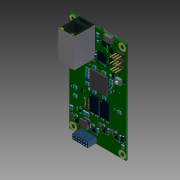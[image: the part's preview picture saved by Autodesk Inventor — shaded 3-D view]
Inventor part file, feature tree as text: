
AUTODESK INVENTOR PART (.ipt)
format: ipt  version: 2013 (Build 170138000, 138)  size: 6,881,792 bytes
history: native  units: in
note: dims shown in document units (in); Inventor stores cm internally (conversion verified against a paired STEP export)
features: imported_body x1163, extrude x1112, other x52, projected_geometry x21, sketch x2
ambient origin geometry x8: Origin, YZ Plane, XZ Plane, XY Plane, X Axis, Y Axis, Z Axis, Center Point
feature tree (2350):
  other  "Board"
  other  "Repaired Geometry1"
  sketch  "Sketch1"  dims[d3=0.3009in d4=0.0005in d5=0.0653in d6=0.0653in d7=0.0653in d8=0.0653in d9=0.0653in d10=0.0653in d11=0.0653in d12=0.0653in d13=0.0098in d14=0.0098in d15=1.1299in d16=1.1299in d17=1.7402in d18=0.0404in]
  extrude  "Extruded"  Depth=0.0005in
  extrude  "Extruded_1"  Depth=0.0653in
  extrude  "Extruded_2"  Depth=0.0653in
  extrude  "Extruded_3"  Depth=0.0653in
  extrude  "Extruded_4"  Depth=0.0653in
  extrude  "Extruded_5"  Depth=0.0653in
  extrude  "Extruded_6"  Depth=0.0653in
  extrude  "Extruded_7"  Depth=0.0653in
  extrude  "Extruded_8"  Depth=0.0653in
  extrude  "Extruded_9"  Depth=0.0098in
  extrude  "Extruded_10"  Depth=0.0098in
  extrude  "Extruded_11"  Depth=1.1299in
  extrude  "Extruded_12"  Depth=1.1299in
  extrude  "Extruded_13"  Depth=1.7402in
  extrude  "Extruded_14"  Depth=0.0404in
  extrude  "Extruded_15"  [1 undecoded]
  extrude  "Extruded_16"  [1 undecoded]
  extrude  "Extruded_17"  [1 undecoded]
  extrude  "Extruded_18"  [1 undecoded]
  extrude  "Extruded_19"  [1 undecoded]
  extrude  "Extruded_20"  [1 undecoded]
  extrude  "Extruded_21"  [1 undecoded]
  extrude  "Extruded_22"  [1 undecoded]
  extrude  "Extruded_23"  [1 undecoded]
  extrude  "Extruded_24"  [1 undecoded]
  extrude  "Extruded_25"  [1 undecoded]
  extrude  "Extruded_26"  [1 undecoded]
  extrude  "Extruded_27"  [1 undecoded]
  other  "Cylinder"
  other  "Cylinder_1"
  other  "Cylinder_2"
  other  "Cylinder_3"
  extrude  "Extruded_28"  [1 undecoded]
  extrude  "Extruded_29"  [1 undecoded]
  other  "Cylinder_4"
  extrude  "Extruded_30"  [1 undecoded]
  other  "Cylinder_5"
  extrude  "Extruded_31"  [1 undecoded]
  other  "Cylinder_6"
  other  "Cylinder_7"
  extrude  "Extruded_32"  [1 undecoded]
  extrude  "Extruded_33"  [1 undecoded]
  extrude  "Extruded_34"  [1 undecoded]
  extrude  "Extruded_35"  [1 undecoded]
  extrude  "Extruded_36"  [1 undecoded]
  extrude  "Extruded_37"  [1 undecoded]
  extrude  "Extruded_38"  [1 undecoded]
  extrude  "Extruded_39"  [1 undecoded]
  extrude  "Extruded_40"  [1 undecoded]
  extrude  "Extruded_41"  [1 undecoded]
  extrude  "Extruded_42"  [1 undecoded]
  extrude  "Extruded_43"  [1 undecoded]
  extrude  "Extruded_44"  [1 undecoded]
  extrude  "Extruded_45"  [1 undecoded]
  extrude  "Extruded_46"  [1 undecoded]
  extrude  "Extruded_47"  [1 undecoded]
  extrude  "Extruded_48"  [1 undecoded]
  extrude  "Extruded_49"  [1 undecoded]
  extrude  "Extruded_50"  [1 undecoded]
  extrude  "Extruded_51"  [1 undecoded]
  extrude  "Extruded_52"  [1 undecoded]
  extrude  "Extruded_53"  [1 undecoded]
  extrude  "Extruded_54"  [1 undecoded]
  extrude  "Extruded_55"  [1 undecoded]
  extrude  "Extruded_56"  [1 undecoded]
  extrude  "Extruded_57"  [1 undecoded]
  extrude  "Extruded_58"  [1 undecoded]
  extrude  "Extruded_59"  [1 undecoded]
  extrude  "Extruded_60"  [1 undecoded]
  extrude  "Extruded_61"  [1 undecoded]
  extrude  "Extruded_62"  [1 undecoded]
  extrude  "Extruded_63"  [1 undecoded]
  extrude  "Extruded_64"  [1 undecoded]
  extrude  "Extruded_65"  [1 undecoded]
  extrude  "Extruded_66"  [1 undecoded]
  extrude  "Extruded_67"  [1 undecoded]
  extrude  "Extruded_68"  [1 undecoded]
  extrude  "Extruded_69"  [1 undecoded]
  extrude  "Extruded_70"  [1 undecoded]
  extrude  "Extruded_71"  [1 undecoded]
  extrude  "Extruded_72"  [1 undecoded]
  extrude  "Extruded_73"  [1 undecoded]
  extrude  "Extruded_74"  [1 undecoded]
  extrude  "Extruded_75"  [1 undecoded]
  extrude  "Extruded_76"  [1 undecoded]
  extrude  "Extruded_77"  [1 undecoded]
  extrude  "Extruded_78"  [1 undecoded]
  extrude  "Extruded_79"  [1 undecoded]
  extrude  "Extruded_80"  [1 undecoded]
  extrude  "Extruded_81"  [1 undecoded]
  extrude  "Extruded_82"  [1 undecoded]
  extrude  "Extruded_83"  [1 undecoded]
  extrude  "Extruded_84"  [1 undecoded]
  extrude  "Extruded_85"  [1 undecoded]
  extrude  "Extruded_86"  [1 undecoded]
  extrude  "Extruded_87"  [1 undecoded]
  extrude  "Extruded_88"  [1 undecoded]
  extrude  "Extruded_89"  [1 undecoded]
  extrude  "Extruded_90"  [1 undecoded]
  extrude  "Extruded_91"  [1 undecoded]
  extrude  "Extruded_92"  [1 undecoded]
  extrude  "Extruded_93"  [1 undecoded]
  extrude  "Extruded_94"  [1 undecoded]
  extrude  "Extruded_95"  [1 undecoded]
  extrude  "Extruded_96"  [1 undecoded]
  extrude  "Extruded_97"  [1 undecoded]
  extrude  "Extruded_98"  [1 undecoded]
  extrude  "Extruded_99"  [1 undecoded]
  extrude  "Extruded_100"  [1 undecoded]
  extrude  "Extruded_101"  [1 undecoded]
  extrude  "Extruded_102"  [1 undecoded]
  extrude  "Extruded_103"  [1 undecoded]
  extrude  "Extruded_104"  [1 undecoded]
  extrude  "Extruded_105"  [1 undecoded]
  extrude  "Extruded_106"  [1 undecoded]
  extrude  "Extruded_107"  [1 undecoded]
  extrude  "Extruded_108"  [1 undecoded]
  extrude  "Extruded_109"  [1 undecoded]
  extrude  "Extruded_110"  [1 undecoded]
  extrude  "Extruded_111"  [1 undecoded]
  extrude  "Extruded_112"  [1 undecoded]
  extrude  "Extruded_113"  [1 undecoded]
  extrude  "Extruded_114"  [1 undecoded]
  extrude  "Extruded_115"  [1 undecoded]
  extrude  "Extruded_116"  [1 undecoded]
  extrude  "Extruded_117"  [1 undecoded]
  extrude  "Extruded_118"  [1 undecoded]
  extrude  "Extruded_119"  [1 undecoded]
  extrude  "Extruded_120"  [1 undecoded]
  extrude  "Extruded_121"  [1 undecoded]
  extrude  "Extruded_122"  [1 undecoded]
  extrude  "Extruded_123"  [1 undecoded]
  extrude  "Extruded_124"  [1 undecoded]
  extrude  "Extruded_125"  [1 undecoded]
  extrude  "Extruded_126"  [1 undecoded]
  extrude  "Extruded_127"  [1 undecoded]
  extrude  "Extruded_128"  [1 undecoded]
  extrude  "Extruded_129"  [1 undecoded]
  extrude  "Extruded_130"  [1 undecoded]
  extrude  "Extruded_131"  [1 undecoded]
  extrude  "Extruded_132"  [1 undecoded]
  extrude  "Extruded_133"  [1 undecoded]
  extrude  "Extruded_134"  [1 undecoded]
  extrude  "Extruded_135"  [1 undecoded]
  extrude  "Extruded_136"  [1 undecoded]
  extrude  "Extruded_137"  [1 undecoded]
  extrude  "Extruded_138"  [1 undecoded]
  extrude  "Extruded_139"  [1 undecoded]
  extrude  "Extruded_140"  [1 undecoded]
  extrude  "Extruded_141"  [1 undecoded]
  extrude  "Extruded_142"  [1 undecoded]
  extrude  "Extruded_143"  [1 undecoded]
  extrude  "Extruded_144"  [1 undecoded]
  extrude  "Extruded_145"  [1 undecoded]
  extrude  "Extruded_146"  [1 undecoded]
  extrude  "Extruded_147"  [1 undecoded]
  extrude  "Extruded_148"  [1 undecoded]
  extrude  "Extruded_149"  [1 undecoded]
  extrude  "Extruded_150"  [1 undecoded]
  extrude  "Extruded_151"  [1 undecoded]
  extrude  "Extruded_152"  [1 undecoded]
  extrude  "Extruded_153"  [1 undecoded]
  extrude  "Extruded_154"  [1 undecoded]
  extrude  "Extruded_155"  [1 undecoded]
  extrude  "Extruded_156"  [1 undecoded]
  extrude  "Extruded_157"  [1 undecoded]
  extrude  "Extruded_158"  [1 undecoded]
  extrude  "Extruded_159"  [1 undecoded]
  extrude  "Extruded_160"  [1 undecoded]
  extrude  "Extruded_161"  [1 undecoded]
  extrude  "Extruded_162"  [1 undecoded]
  extrude  "Extruded_163"  [1 undecoded]
  extrude  "Extruded_164"  [1 undecoded]
  extrude  "Extruded_165"  [1 undecoded]
  extrude  "Extruded_166"  [1 undecoded]
  extrude  "Extruded_167"  [1 undecoded]
  extrude  "Extruded_168"  [1 undecoded]
  extrude  "Extruded_169"  [1 undecoded]
  extrude  "Extruded_170"  [1 undecoded]
  extrude  "Extruded_171"  [1 undecoded]
  extrude  "Extruded_172"  [1 undecoded]
  extrude  "Extruded_173"  [1 undecoded]
  extrude  "Extruded_174"  [1 undecoded]
  extrude  "Extruded_175"  [1 undecoded]
  extrude  "Extruded_176"  [1 undecoded]
  extrude  "Extruded_177"  [1 undecoded]
  extrude  "Extruded_178"  [1 undecoded]
  extrude  "Extruded_179"  [1 undecoded]
  extrude  "Extruded_180"  [1 undecoded]
  extrude  "Extruded_181"  [1 undecoded]
  extrude  "Extruded_182"  [1 undecoded]
  extrude  "Extruded_183"  [1 undecoded]
  extrude  "Extruded_184"  [1 undecoded]
  extrude  "Extruded_185"  [1 undecoded]
  extrude  "Extruded_186"  [1 undecoded]
  extrude  "Extruded_187"  [1 undecoded]
  extrude  "Extruded_188"  [1 undecoded]
  extrude  "Extruded_189"  [1 undecoded]
  extrude  "Extruded_190"  [1 undecoded]
  extrude  "Extruded_191"  [1 undecoded]
  extrude  "Extruded_192"  [1 undecoded]
  extrude  "Extruded_193"  [1 undecoded]
  extrude  "Extruded_194"  [1 undecoded]
  extrude  "Extruded_195"  [1 undecoded]
  extrude  "Extruded_196"  [1 undecoded]
  extrude  "Extruded_197"  [1 undecoded]
  extrude  "Extruded_198"  [1 undecoded]
  extrude  "Extruded_199"  [1 undecoded]
  extrude  "Extruded_200"  [1 undecoded]
  extrude  "Extruded_201"  [1 undecoded]
  extrude  "Extruded_202"  [1 undecoded]
  extrude  "Extruded_203"  [1 undecoded]
  extrude  "Extruded_204"  [1 undecoded]
  extrude  "Extruded_205"  [1 undecoded]
  extrude  "Extruded_206"  [1 undecoded]
  extrude  "Extruded_207"  [1 undecoded]
  extrude  "Extruded_208"  [1 undecoded]
  extrude  "Extruded_209"  [1 undecoded]
  extrude  "Extruded_210"  [1 undecoded]
  extrude  "Extruded_211"  [1 undecoded]
  extrude  "Extruded_212"  [1 undecoded]
  extrude  "Extruded_213"  [1 undecoded]
  extrude  "Extruded_214"  [1 undecoded]
  extrude  "Extruded_215"  [1 undecoded]
  extrude  "Extruded_216"  [1 undecoded]
  extrude  "Extruded_217"  [1 undecoded]
  extrude  "Extruded_218"  [1 undecoded]
  extrude  "Extruded_219"  [1 undecoded]
  extrude  "Extruded_220"  [1 undecoded]
  extrude  "Extruded_221"  [1 undecoded]
  extrude  "Extruded_222"  [1 undecoded]
  extrude  "Extruded_223"  [1 undecoded]
  extrude  "Extruded_224"  [1 undecoded]
  extrude  "Extruded_225"  [1 undecoded]
  extrude  "Extruded_226"  [1 undecoded]
  extrude  "Extruded_227"  [1 undecoded]
  extrude  "Extruded_228"  [1 undecoded]
  extrude  "Extruded_229"  [1 undecoded]
  extrude  "Extruded_230"  [1 undecoded]
  extrude  "Extruded_231"  [1 undecoded]
  extrude  "Extruded_232"  [1 undecoded]
  extrude  "Extruded_233"  [1 undecoded]
  extrude  "Extruded_234"  [1 undecoded]
  extrude  "Extruded_235"  [1 undecoded]
  extrude  "Extruded_236"  [1 undecoded]
  extrude  "Extruded_237"  [1 undecoded]
  extrude  "Extruded_238"  [1 undecoded]
  extrude  "Extruded_239"  [1 undecoded]
  extrude  "Extruded_240"  [1 undecoded]
  extrude  "Extruded_241"  [1 undecoded]
  extrude  "Extruded_242"  [1 undecoded]
  extrude  "Extruded_243"  [1 undecoded]
  extrude  "Extruded_244"  [1 undecoded]
  extrude  "Extruded_245"  [1 undecoded]
  extrude  "Extruded_246"  [1 undecoded]
  extrude  "Extruded_247"  [1 undecoded]
  extrude  "Extruded_248"  [1 undecoded]
  extrude  "Extruded_249"  [1 undecoded]
  extrude  "Extruded_250"  [1 undecoded]
  extrude  "Extruded_251"  [1 undecoded]
  extrude  "Extruded_252"  [1 undecoded]
  extrude  "Extruded_253"  [1 undecoded]
  extrude  "Extruded_254"  [1 undecoded]
  extrude  "Extruded_255"  [1 undecoded]
  extrude  "Extruded_256"  [1 undecoded]
  extrude  "Extruded_257"  [1 undecoded]
  extrude  "Extruded_258"  [1 undecoded]
  extrude  "Extruded_259"  [1 undecoded]
  extrude  "Extruded_260"  [1 undecoded]
  extrude  "Extruded_261"  [1 undecoded]
  extrude  "Extruded_262"  [1 undecoded]
  extrude  "Extruded_263"  [1 undecoded]
  extrude  "Extruded_264"  [1 undecoded]
  extrude  "Extruded_265"  [1 undecoded]
  extrude  "Extruded_266"  [1 undecoded]
  extrude  "Extruded_267"  [1 undecoded]
  extrude  "Extruded_268"  [1 undecoded]
  extrude  "Extruded_269"  [1 undecoded]
  extrude  "Extruded_270"  [1 undecoded]
  extrude  "Extruded_271"  [1 undecoded]
  extrude  "Extruded_272"  [1 undecoded]
  extrude  "Extruded_273"  [1 undecoded]
  extrude  "Extruded_274"  [1 undecoded]
  extrude  "Extruded_275"  [1 undecoded]
  extrude  "Extruded_276"  [1 undecoded]
  extrude  "Extruded_277"  [1 undecoded]
  extrude  "Extruded_278"  [1 undecoded]
  extrude  "Extruded_279"  [1 undecoded]
  extrude  "Extruded_280"  [1 undecoded]
  extrude  "Extruded_281"  [1 undecoded]
  extrude  "Extruded_282"  [1 undecoded]
  extrude  "Extruded_283"  [1 undecoded]
  extrude  "Extruded_284"  [1 undecoded]
  extrude  "Extruded_285"  [1 undecoded]
  extrude  "Extruded_286"  [1 undecoded]
  extrude  "Extruded_287"  [1 undecoded]
  extrude  "Extruded_288"  [1 undecoded]
  extrude  "Extruded_289"  [1 undecoded]
  extrude  "Extruded_290"  [1 undecoded]
  extrude  "Extruded_291"  [1 undecoded]
  extrude  "Extruded_292"  [1 undecoded]
  extrude  "Extruded_293"  [1 undecoded]
  extrude  "Extruded_294"  [1 undecoded]
  extrude  "Extruded_295"  [1 undecoded]
  extrude  "Extruded_296"  [1 undecoded]
  extrude  "Extruded_297"  [1 undecoded]
  extrude  "Extruded_298"  [1 undecoded]
  extrude  "Extruded_299"  [1 undecoded]
  extrude  "Extruded_300"  [1 undecoded]
  extrude  "Extruded_301"  [1 undecoded]
  extrude  "Extruded_302"  [1 undecoded]
  extrude  "Extruded_303"  [1 undecoded]
  extrude  "Extruded_304"  [1 undecoded]
  extrude  "Extruded_305"  [1 undecoded]
  extrude  "Extruded_306"  [1 undecoded]
  extrude  "Extruded_307"  [1 undecoded]
  extrude  "Extruded_308"  [1 undecoded]
  extrude  "Extruded_309"  [1 undecoded]
  extrude  "Extruded_310"  [1 undecoded]
  extrude  "Extruded_311"  [1 undecoded]
  extrude  "Extruded_312"  [1 undecoded]
  extrude  "Extruded_313"  [1 undecoded]
  extrude  "Extruded_314"  [1 undecoded]
  extrude  "Extruded_315"  [1 undecoded]
  extrude  "Extruded_316"  [1 undecoded]
  extrude  "Extruded_317"  [1 undecoded]
  extrude  "Extruded_318"  [1 undecoded]
  extrude  "Extruded_319"  [1 undecoded]
  extrude  "Extruded_320"  [1 undecoded]
  extrude  "Extruded_321"  [1 undecoded]
  extrude  "Extruded_322"  [1 undecoded]
  extrude  "Extruded_323"  [1 undecoded]
  extrude  "Extruded_324"  [1 undecoded]
  extrude  "Extruded_325"  [1 undecoded]
  extrude  "Extruded_326"  [1 undecoded]
  extrude  "Extruded_327"  [1 undecoded]
  extrude  "Extruded_328"  [1 undecoded]
  extrude  "Extruded_329"  [1 undecoded]
  extrude  "Extruded_330"  [1 undecoded]
  extrude  "Extruded_331"  [1 undecoded]
  extrude  "Extruded_332"  [1 undecoded]
  extrude  "Extruded_333"  [1 undecoded]
  extrude  "Extruded_334"  [1 undecoded]
  extrude  "Extruded_335"  [1 undecoded]
  extrude  "Extruded_336"  [1 undecoded]
  extrude  "Extruded_337"  [1 undecoded]
  extrude  "Extruded_338"  [1 undecoded]
  extrude  "Extruded_339"  [1 undecoded]
  extrude  "Extruded_340"  [1 undecoded]
  extrude  "Extruded_341"  [1 undecoded]
  extrude  "Extruded_342"  [1 undecoded]
  extrude  "Extruded_343"  [1 undecoded]
  extrude  "Extruded_344"  [1 undecoded]
  extrude  "Extruded_345"  [1 undecoded]
  extrude  "Extruded_346"  [1 undecoded]
  extrude  "Extruded_347"  [1 undecoded]
  extrude  "Extruded_348"  [1 undecoded]
  extrude  "Extruded_349"  [1 undecoded]
  extrude  "Extruded_350"  [1 undecoded]
  extrude  "Extruded_351"  [1 undecoded]
  extrude  "Extruded_352"  [1 undecoded]
  extrude  "Extruded_353"  [1 undecoded]
  extrude  "Extruded_354"  [1 undecoded]
  extrude  "Extruded_355"  [1 undecoded]
  extrude  "Extruded_356"  [1 undecoded]
  extrude  "Extruded_357"  [1 undecoded]
  extrude  "Extruded_358"  [1 undecoded]
  extrude  "Extruded_359"  [1 undecoded]
  extrude  "Extruded_360"  [1 undecoded]
  extrude  "Extruded_361"  [1 undecoded]
  extrude  "Extruded_362"  [1 undecoded]
  extrude  "Extruded_363"  [1 undecoded]
  extrude  "Extruded_364"  [1 undecoded]
  extrude  "Extruded_365"  [1 undecoded]
  extrude  "Extruded_366"  [1 undecoded]
  extrude  "Extruded_367"  [1 undecoded]
  extrude  "Extruded_368"  [1 undecoded]
  extrude  "Extruded_369"  [1 undecoded]
  extrude  "Extruded_370"  [1 undecoded]
  extrude  "Extruded_371"  [1 undecoded]
  extrude  "Extruded_372"  [1 undecoded]
  extrude  "Extruded_373"  [1 undecoded]
  extrude  "Extruded_374"  [1 undecoded]
  extrude  "Extruded_375"  [1 undecoded]
  extrude  "Extruded_376"  [1 undecoded]
  extrude  "Extruded_377"  [1 undecoded]
  extrude  "Extruded_378"  [1 undecoded]
  extrude  "Extruded_379"  [1 undecoded]
  extrude  "Extruded_380"  [1 undecoded]
  extrude  "Extruded_381"  [1 undecoded]
  extrude  "Extruded_382"  [1 undecoded]
  extrude  "Extruded_383"  [1 undecoded]
  extrude  "Extruded_384"  [1 undecoded]
  extrude  "Extruded_385"  [1 undecoded]
  extrude  "Extruded_386"  [1 undecoded]
  extrude  "Extruded_387"  [1 undecoded]
  extrude  "Extruded_388"  [1 undecoded]
  extrude  "Extruded_389"  [1 undecoded]
  extrude  "Extruded_390"  [1 undecoded]
  extrude  "Extruded_391"  [1 undecoded]
  extrude  "Extruded_392"  [1 undecoded]
  extrude  "Extruded_393"  [1 undecoded]
  extrude  "Extruded_394"  [1 undecoded]
  extrude  "Extruded_395"  [1 undecoded]
  extrude  "Extruded_396"  [1 undecoded]
  extrude  "Extruded_397"  [1 undecoded]
  extrude  "Extruded_398"  [1 undecoded]
  extrude  "Extruded_399"  [1 undecoded]
  extrude  "Extruded_400"  [1 undecoded]
  extrude  "Extruded_401"  [1 undecoded]
  extrude  "Extruded_402"  [1 undecoded]
  extrude  "Extruded_403"  [1 undecoded]
  extrude  "Extruded_404"  [1 undecoded]
  extrude  "Extruded_405"  [1 undecoded]
  extrude  "Extruded_406"  [1 undecoded]
  extrude  "Extruded_407"  [1 undecoded]
  extrude  "Extruded_408"  [1 undecoded]
  extrude  "Extruded_409"  [1 undecoded]
  extrude  "Extruded_410"  [1 undecoded]
  extrude  "Extruded_411"  [1 undecoded]
  extrude  "Extruded_412"  [1 undecoded]
  extrude  "Extruded_413"  [1 undecoded]
  extrude  "Extruded_414"  [1 undecoded]
  extrude  "Extruded_415"  [1 undecoded]
  extrude  "Extruded_416"  [1 undecoded]
  extrude  "Extruded_417"  [1 undecoded]
  extrude  "Extruded_418"  [1 undecoded]
  extrude  "Extruded_419"  [1 undecoded]
  extrude  "Extruded_420"  [1 undecoded]
  extrude  "Extruded_421"  [1 undecoded]
  extrude  "Extruded_422"  [1 undecoded]
  extrude  "Extruded_423"  [1 undecoded]
  extrude  "Extruded_424"  [1 undecoded]
  extrude  "Extruded_425"  [1 undecoded]
  extrude  "Extruded_426"  [1 undecoded]
  extrude  "Extruded_427"  [1 undecoded]
  extrude  "Extruded_428"  [1 undecoded]
  extrude  "Extruded_429"  [1 undecoded]
  extrude  "Extruded_430"  [1 undecoded]
  extrude  "Extruded_431"  [1 undecoded]
  extrude  "Extruded_432"  [1 undecoded]
  extrude  "Extruded_433"  [1 undecoded]
  extrude  "Extruded_434"  [1 undecoded]
  extrude  "Extruded_435"  [1 undecoded]
  extrude  "Extruded_436"  [1 undecoded]
  extrude  "Extruded_437"  [1 undecoded]
  extrude  "Extruded_438"  [1 undecoded]
  extrude  "Extruded_439"  [1 undecoded]
  extrude  "Extruded_440"  [1 undecoded]
  extrude  "Extruded_441"  [1 undecoded]
  extrude  "Extruded_442"  [1 undecoded]
  extrude  "Extruded_443"  [1 undecoded]
  extrude  "Extruded_444"  [1 undecoded]
  extrude  "Extruded_445"  [1 undecoded]
  extrude  "Extruded_446"  [1 undecoded]
  extrude  "Extruded_447"  [1 undecoded]
  extrude  "Extruded_448"  [1 undecoded]
  extrude  "Extruded_449"  [1 undecoded]
  extrude  "Extruded_450"  [1 undecoded]
  extrude  "Extruded_451"  [1 undecoded]
  extrude  "Extruded_452"  [1 undecoded]
  extrude  "Extruded_453"  [1 undecoded]
  extrude  "Extruded_454"  [1 undecoded]
  extrude  "Extruded_455"  [1 undecoded]
  extrude  "Extruded_456"  [1 undecoded]
  extrude  "Extruded_457"  [1 undecoded]
  extrude  "Extruded_458"  [1 undecoded]
  extrude  "Extruded_459"  [1 undecoded]
  extrude  "Extruded_460"  [1 undecoded]
  extrude  "Extruded_461"  [1 undecoded]
  extrude  "Extruded_462"  [1 undecoded]
  extrude  "Extruded_463"  [1 undecoded]
  extrude  "Extruded_464"  [1 undecoded]
  extrude  "Extruded_465"  [1 undecoded]
  extrude  "Extruded_466"  [1 undecoded]
  extrude  "Extruded_467"  [1 undecoded]
  extrude  "Extruded_468"  [1 undecoded]
  extrude  "Extruded_469"  [1 undecoded]
  extrude  "Extruded_470"  [1 undecoded]
  extrude  "Extruded_471"  [1 undecoded]
  extrude  "Extruded_472"  [1 undecoded]
  extrude  "Extruded_473"  [1 undecoded]
  extrude  "Extruded_474"  [1 undecoded]
  extrude  "Extruded_475"  [1 undecoded]
  extrude  "Extruded_476"  [1 undecoded]
  extrude  "Extruded_477"  [1 undecoded]
  extrude  "Extruded_478"  [1 undecoded]
  extrude  "Extruded_479"  [1 undecoded]
  extrude  "Extruded_480"  [1 undecoded]
  extrude  "Extruded_481"  [1 undecoded]
  extrude  "Extruded_482"  [1 undecoded]
  extrude  "Extruded_483"  [1 undecoded]
  extrude  "Extruded_484"  [1 undecoded]
  extrude  "Extruded_485"  [1 undecoded]
  extrude  "Extruded_486"  [1 undecoded]
  extrude  "Extruded_487"  [1 undecoded]
  extrude  "Extruded_488"  [1 undecoded]
  extrude  "Extruded_489"  [1 undecoded]
  extrude  "Extruded_490"  [1 undecoded]
  extrude  "Extruded_491"  [1 undecoded]
  extrude  "Extruded_492"  [1 undecoded]
  extrude  "Extruded_493"  [1 undecoded]
  extrude  "Extruded_494"  [1 undecoded]
  extrude  "Extruded_495"  [1 undecoded]
  extrude  "Extruded_496"  [1 undecoded]
  extrude  "Extruded_497"  [1 undecoded]
  extrude  "Extruded_498"  [1 undecoded]
  extrude  "Extruded_499"  [1 undecoded]
  extrude  "Extruded_500"  [1 undecoded]
  extrude  "Extruded_501"  [1 undecoded]
  extrude  "Extruded_502"  [1 undecoded]
  extrude  "Extruded_503"  [1 undecoded]
  extrude  "Extruded_504"  [1 undecoded]
  extrude  "Extruded_505"  [1 undecoded]
  extrude  "Extruded_506"  [1 undecoded]
  extrude  "Extruded_507"  [1 undecoded]
  extrude  "Extruded_508"  [1 undecoded]
  extrude  "Extruded_509"  [1 undecoded]
  extrude  "Extruded_510"  [1 undecoded]
  extrude  "Extruded_511"  [1 undecoded]
  extrude  "Extruded_512"  [1 undecoded]
  extrude  "Extruded_513"  [1 undecoded]
  extrude  "Extruded_514"  [1 undecoded]
  extrude  "Extruded_515"  [1 undecoded]
  extrude  "Extruded_516"  [1 undecoded]
  extrude  "Extruded_517"  [1 undecoded]
  extrude  "Extruded_518"  [1 undecoded]
  extrude  "Extruded_519"  [1 undecoded]
  extrude  "Extruded_520"  [1 undecoded]
  extrude  "Extruded_521"  [1 undecoded]
  extrude  "Extruded_522"  [1 undecoded]
  extrude  "Extruded_523"  [1 undecoded]
  extrude  "Extruded_524"  [1 undecoded]
  extrude  "Extruded_525"  [1 undecoded]
  extrude  "Extruded_526"  [1 undecoded]
  extrude  "Extruded_527"  [1 undecoded]
  extrude  "Extruded_528"  [1 undecoded]
  extrude  "Extruded_529"  [1 undecoded]
  extrude  "Extruded_530"  [1 undecoded]
  extrude  "Extruded_531"  [1 undecoded]
  extrude  "Extruded_532"  [1 undecoded]
  extrude  "Extruded_533"  [1 undecoded]
  extrude  "Extruded_534"  [1 undecoded]
  extrude  "Extruded_535"  [1 undecoded]
  extrude  "Extruded_536"  [1 undecoded]
  extrude  "Extruded_537"  [1 undecoded]
  extrude  "Extruded_538"  [1 undecoded]
  extrude  "Extruded_539"  [1 undecoded]
  extrude  "Extruded_540"  [1 undecoded]
  extrude  "Extruded_541"  [1 undecoded]
  extrude  "Extruded_542"  [1 undecoded]
  extrude  "Extruded_543"  [1 undecoded]
  extrude  "Extruded_544"  [1 undecoded]
  extrude  "Extruded_545"  [1 undecoded]
  extrude  "Extruded_546"  [1 undecoded]
  extrude  "Extruded_547"  [1 undecoded]
  extrude  "Extruded_548"  [1 undecoded]
  extrude  "Extruded_549"  [1 undecoded]
  extrude  "Extruded_550"  [1 undecoded]
  extrude  "Extruded_551"  [1 undecoded]
  extrude  "Extruded_552"  [1 undecoded]
  extrude  "Extruded_553"  [1 undecoded]
  extrude  "Extruded_554"  [1 undecoded]
  extrude  "Extruded_555"  [1 undecoded]
  extrude  "Extruded_556"  [1 undecoded]
  extrude  "Extruded_557"  [1 undecoded]
  extrude  "Extruded_558"  [1 undecoded]
  extrude  "Extruded_559"  [1 undecoded]
  extrude  "Extruded_560"  [1 undecoded]
  extrude  "Extruded_561"  [1 undecoded]
  extrude  "Extruded_562"  [1 undecoded]
  extrude  "Extruded_563"  [1 undecoded]
  extrude  "Extruded_564"  [1 undecoded]
  extrude  "Extruded_565"  [1 undecoded]
  extrude  "Extruded_566"  [1 undecoded]
  extrude  "Extruded_567"  [1 undecoded]
  extrude  "Extruded_568"  [1 undecoded]
  extrude  "Extruded_569"  [1 undecoded]
  extrude  "Extruded_570"  [1 undecoded]
  extrude  "Extruded_571"  [1 undecoded]
  extrude  "Extruded_572"  [1 undecoded]
  extrude  "Extruded_573"  [1 undecoded]
  extrude  "Extruded_574"  [1 undecoded]
  extrude  "Extruded_575"  [1 undecoded]
  extrude  "Extruded_576"  [1 undecoded]
  extrude  "Extruded_577"  [1 undecoded]
  extrude  "Extruded_578"  [1 undecoded]
  extrude  "Extruded_579"  [1 undecoded]
  extrude  "Extruded_580"  [1 undecoded]
  extrude  "Extruded_581"  [1 undecoded]
  extrude  "Extruded_582"  [1 undecoded]
  extrude  "Extruded_583"  [1 undecoded]
  extrude  "Extruded_584"  [1 undecoded]
  extrude  "Extruded_585"  [1 undecoded]
  extrude  "Extruded_586"  [1 undecoded]
  extrude  "Extruded_587"  [1 undecoded]
  extrude  "Extruded_588"  [1 undecoded]
  extrude  "Extruded_589"  [1 undecoded]
  extrude  "Extruded_590"  [1 undecoded]
  extrude  "Extruded_591"  [1 undecoded]
  extrude  "Extruded_592"  [1 undecoded]
  extrude  "Extruded_593"  [1 undecoded]
  extrude  "Extruded_594"  [1 undecoded]
  extrude  "Extruded_595"  [1 undecoded]
  extrude  "Extruded_596"  [1 undecoded]
  extrude  "Extruded_597"  [1 undecoded]
  extrude  "Extruded_598"  [1 undecoded]
  extrude  "Extruded_599"  [1 undecoded]
  extrude  "Extruded_600"  [1 undecoded]
  extrude  "Extruded_601"  [1 undecoded]
  extrude  "Extruded_602"  [1 undecoded]
  extrude  "Extruded_603"  [1 undecoded]
  extrude  "Extruded_604"  [1 undecoded]
  extrude  "Extruded_605"  [1 undecoded]
  extrude  "Extruded_606"  [1 undecoded]
  extrude  "Extruded_607"  [1 undecoded]
  extrude  "Extruded_608"  [1 undecoded]
  extrude  "Extruded_609"  [1 undecoded]
  extrude  "Extruded_610"  [1 undecoded]
  extrude  "Extruded_611"  [1 undecoded]
  extrude  "Extruded_612"  [1 undecoded]
  extrude  "Extruded_613"  [1 undecoded]
  extrude  "Extruded_614"  [1 undecoded]
  extrude  "Extruded_615"  [1 undecoded]
  extrude  "Extruded_616"  [1 undecoded]
  extrude  "Extruded_617"  [1 undecoded]
  extrude  "Extruded_618"  [1 undecoded]
  extrude  "Extruded_619"  [1 undecoded]
  extrude  "Extruded_620"  [1 undecoded]
  extrude  "Extruded_621"  [1 undecoded]
  extrude  "Extruded_622"  [1 undecoded]
  extrude  "Extruded_623"  [1 undecoded]
  extrude  "Extruded_624"  [1 undecoded]
  extrude  "Extruded_625"  [1 undecoded]
  extrude  "Extruded_626"  [1 undecoded]
  extrude  "Extruded_627"  [1 undecoded]
  extrude  "Extruded_628"  [1 undecoded]
  extrude  "Extruded_629"  [1 undecoded]
  extrude  "Extruded_630"  [1 undecoded]
  extrude  "Extruded_631"  [1 undecoded]
  extrude  "Extruded_632"  [1 undecoded]
  extrude  "Extruded_633"  [1 undecoded]
  extrude  "Extruded_634"  [1 undecoded]
  extrude  "Extruded_635"  [1 undecoded]
  extrude  "Extruded_636"  [1 undecoded]
  extrude  "Extruded_637"  [1 undecoded]
  extrude  "Extruded_638"  [1 undecoded]
  extrude  "Extruded_639"  [1 undecoded]
  extrude  "Extruded_640"  [1 undecoded]
  extrude  "Extruded_641"  [1 undecoded]
  other  "Cylinder_8"
  extrude  "Extruded_642"  [1 undecoded]
  extrude  "Extruded_643"  [1 undecoded]
  extrude  "Extruded_644"  [1 undecoded]
  extrude  "Extruded_645"  [1 undecoded]
  extrude  "Extruded_646"  [1 undecoded]
  extrude  "Extruded_647"  [1 undecoded]
  extrude  "Extruded_648"  [1 undecoded]
  extrude  "Extruded_649"  [1 undecoded]
  extrude  "Extruded_650"  [1 undecoded]
  extrude  "Extruded_651"  [1 undecoded]
  extrude  "Extruded_652"  [1 undecoded]
  extrude  "Extruded_653"  [1 undecoded]
  extrude  "Extruded_654"  [1 undecoded]
  extrude  "Extruded_655"  [1 undecoded]
  extrude  "Extruded_656"  [1 undecoded]
  extrude  "Extruded_657"  [1 undecoded]
  extrude  "Extruded_658"  [1 undecoded]
  extrude  "Extruded_659"  [1 undecoded]
  extrude  "Extruded_660"  [1 undecoded]
  extrude  "Extruded_661"  [1 undecoded]
  extrude  "Extruded_662"  [1 undecoded]
  extrude  "Extruded_663"  [1 undecoded]
  extrude  "Extruded_664"  [1 undecoded]
  other  "Open CASCADE STEP translator 6.2 1.226.1.1"
  extrude  "Extruded_665"  [1 undecoded]
  extrude  "Extruded_666"  [1 undecoded]
  extrude  "Extruded_667"  [1 undecoded]
  extrude  "Extruded_668"  [1 undecoded]
  extrude  "Extruded_669"  [1 undecoded]
  extrude  "Extruded_670"  [1 undecoded]
  extrude  "Extruded_671"  [1 undecoded]
  extrude  "Extruded_672"  [1 undecoded]
  extrude  "Extruded_673"  [1 undecoded]
  extrude  "Extruded_674"  [1 undecoded]
  extrude  "Extruded_675"  [1 undecoded]
  extrude  "Extruded_676"  [1 undecoded]
  extrude  "Extruded_677"  [1 undecoded]
  extrude  "Extruded_678"  [1 undecoded]
  extrude  "Extruded_679"  [1 undecoded]
  extrude  "Extruded_680"  [1 undecoded]
  extrude  "Extruded_681"  [1 undecoded]
  extrude  "Extruded_682"  [1 undecoded]
  extrude  "Extruded_683"  [1 undecoded]
  extrude  "Extruded_684"  [1 undecoded]
  extrude  "Extruded_685"  [1 undecoded]
  extrude  "Extruded_686"  [1 undecoded]
  extrude  "Extruded_687"  [1 undecoded]
  extrude  "Extruded_688"  [1 undecoded]
  extrude  "Extruded_689"  [1 undecoded]
  extrude  "Extruded_690"  [1 undecoded]
  extrude  "Extruded_691"  [1 undecoded]
  extrude  "Extruded_692"  [1 undecoded]
  extrude  "Extruded_693"  [1 undecoded]
  extrude  "Extruded_694"  [1 undecoded]
  extrude  "Extruded_695"  [1 undecoded]
  extrude  "Extruded_696"  [1 undecoded]
  extrude  "Extruded_697"  [1 undecoded]
  extrude  "Extruded_698"  [1 undecoded]
  extrude  "Extruded_699"  [1 undecoded]
  extrude  "Extruded_700"  [1 undecoded]
  extrude  "Extruded_701"  [1 undecoded]
  extrude  "Extruded_702"  [1 undecoded]
  extrude  "Extruded_703"  [1 undecoded]
  extrude  "Extruded_704"  [1 undecoded]
  other  "Cylinder_9"
  other  "Cylinder_10"
  other  "Cylinder_11"
  other  "Cylinder_12"
  other  "Cylinder_13"
  other  "Cylinder_14"
  other  "Cylinder_15"
  other  "Cylinder_16"
  other  "Cylinder_17"
  other  "Cylinder_18"
  other  "Cylinder_19"
  other  "Cylinder_20"
  other  "Cylinder_21"
  other  "Cylinder_22"
  other  "Cylinder_23"
  other  "Cylinder_24"
  other  "Cylinder_25"
  other  "Cylinder_26"
  other  "Cylinder_27"
  other  "Cylinder_28"
  extrude  "Extruded_705"  [1 undecoded]
  other  "Cylinder_29"
  other  "Cylinder_30"
  extrude  "Extruded_706"  [1 undecoded]
  extrude  "Extruded_707"  [1 undecoded]
  extrude  "Extruded_708"  [1 undecoded]
  extrude  "Extruded_709"  [1 undecoded]
  extrude  "Extruded_710"  [1 undecoded]
  extrude  "Extruded_711"  [1 undecoded]
  extrude  "Extruded_712"  [1 undecoded]
  extrude  "Extruded_713"  [1 undecoded]
  extrude  "Extruded_714"  [1 undecoded]
  extrude  "Extruded_715"  [1 undecoded]
  extrude  "Extruded_716"  [1 undecoded]
  extrude  "Extruded_717"  [1 undecoded]
  extrude  "Extruded_718"  [1 undecoded]
  extrude  "Extruded_719"  [1 undecoded]
  extrude  "Extruded_720"  [1 undecoded]
  extrude  "Extruded_721"  [1 undecoded]
  extrude  "Extruded_722"  [1 undecoded]
  other  "Open CASCADE STEP translator 6.2 1.229.1.1"
  extrude  "Extruded_723"  [1 undecoded]
  extrude  "Extruded_724"  [1 undecoded]
  extrude  "Extruded_725"  [1 undecoded]
  extrude  "Extruded_726"  [1 undecoded]
  extrude  "Extruded_727"  [1 undecoded]
  extrude  "Extruded_728"  [1 undecoded]
  extrude  "Extruded_729"  [1 undecoded]
  extrude  "Extruded_730"  [1 undecoded]
  extrude  "Extruded_731"  [1 undecoded]
  extrude  "Extruded_732"  [1 undecoded]
  extrude  "Extruded_733"  [1 undecoded]
  extrude  "Extruded_734"  [1 undecoded]
  other  "61082101400lf"
  other  "61082101400lf_1"
  extrude  "Extruded_735"  [1 undecoded]
  extrude  "Extruded_736"  [1 undecoded]
  extrude  "Extruded_737"  [1 undecoded]
  extrude  "Extruded_738"  [1 undecoded]
  extrude  "Extruded_739"  [1 undecoded]
  extrude  "Extruded_740"  [1 undecoded]
  extrude  "Extruded_741"  [1 undecoded]
  extrude  "Extruded_742"  [1 undecoded]
  extrude  "Extruded_743"  [1 undecoded]
  extrude  "Extruded_744"  [1 undecoded]
  extrude  "Extruded_745"  [1 undecoded]
  extrude  "Extruded_746"  [1 undecoded]
  extrude  "Extruded_747"  [1 undecoded]
  extrude  "Extruded_748"  [1 undecoded]
  extrude  "Extruded_749"  [1 undecoded]
  extrude  "Extruded_750"  [1 undecoded]
  extrude  "Extruded_751"  [1 undecoded]
  extrude  "Extruded_752"  [1 undecoded]
  extrude  "Extruded_753"  [1 undecoded]
  extrude  "Extruded_754"  [1 undecoded]
  extrude  "Extruded_755"  [1 undecoded]
  extrude  "Extruded_756"  [1 undecoded]
  extrude  "Extruded_757"  [1 undecoded]
  extrude  "Extruded_758"  [1 undecoded]
  extrude  "Extruded_759"  [1 undecoded]
  extrude  "Extruded_760"  [1 undecoded]
  extrude  "Extruded_761"  [1 undecoded]
  extrude  "Extruded_762"  [1 undecoded]
  extrude  "Extruded_763"  [1 undecoded]
  extrude  "Extruded_764"  [1 undecoded]
  extrude  "Extruded_765"  [1 undecoded]
  extrude  "Extruded_766"  [1 undecoded]
  extrude  "Extruded_767"  [1 undecoded]
  extrude  "Extruded_768"  [1 undecoded]
  extrude  "Extruded_769"  [1 undecoded]
  extrude  "Extruded_770"  [1 undecoded]
  extrude  "Extruded_771"  [1 undecoded]
  extrude  "Extruded_772"  [1 undecoded]
  extrude  "Extruded_773"  [1 undecoded]
  extrude  "Extruded_774"  [1 undecoded]
  extrude  "Extruded_775"  [1 undecoded]
  extrude  "Extruded_776"  [1 undecoded]
  extrude  "Extruded_777"  [1 undecoded]
  extrude  "Extruded_778"  [1 undecoded]
  extrude  "Extruded_779"  [1 undecoded]
  extrude  "Extruded_780"  [1 undecoded]
  extrude  "Extruded_781"  [1 undecoded]
  extrude  "Extruded_782"  [1 undecoded]
  extrude  "Extruded_783"  [1 undecoded]
  extrude  "Extruded_784"  [1 undecoded]
  extrude  "Extruded_785"  [1 undecoded]
  extrude  "Extruded_786"  [1 undecoded]
  extrude  "Extruded_787"  [1 undecoded]
  extrude  "Extruded_788"  [1 undecoded]
  extrude  "Extruded_789"  [1 undecoded]
  extrude  "Extruded_790"  [1 undecoded]
  extrude  "Extruded_791"  [1 undecoded]
  extrude  "Extruded_792"  [1 undecoded]
  extrude  "Extruded_793"  [1 undecoded]
  extrude  "Extruded_794"  [1 undecoded]
  extrude  "Extruded_795"  [1 undecoded]
  extrude  "Extruded_796"  [1 undecoded]
  extrude  "Extruded_797"  [1 undecoded]
  extrude  "Extruded_798"  [1 undecoded]
  extrude  "Extruded_799"  [1 undecoded]
  extrude  "Extruded_800"  [1 undecoded]
  extrude  "Extruded_801"  [1 undecoded]
  extrude  "Extruded_802"  [1 undecoded]
  extrude  "Extruded_803"  [1 undecoded]
  extrude  "Extruded_804"  [1 undecoded]
  extrude  "Extruded_805"  [1 undecoded]
  extrude  "Extruded_806"  [1 undecoded]
  extrude  "Extruded_807"  [1 undecoded]
  extrude  "Extruded_808"  [1 undecoded]
  extrude  "Extruded_809"  [1 undecoded]
  extrude  "Extruded_810"  [1 undecoded]
  extrude  "Extruded_811"  [1 undecoded]
  extrude  "Extruded_812"  [1 undecoded]
  extrude  "Extruded_813"  [1 undecoded]
  extrude  "Extruded_814"  [1 undecoded]
  extrude  "Extruded_815"  [1 undecoded]
  extrude  "Extruded_816"  [1 undecoded]
  extrude  "Extruded_817"  [1 undecoded]
  extrude  "Extruded_818"  [1 undecoded]
  extrude  "Extruded_819"  [1 undecoded]
  extrude  "Extruded_820"  [1 undecoded]
  extrude  "Extruded_821"  [1 undecoded]
  extrude  "Extruded_822"  [1 undecoded]
  extrude  "Extruded_823"  [1 undecoded]
  extrude  "Extruded_824"  [1 undecoded]
  extrude  "Extruded_825"  [1 undecoded]
  extrude  "Extruded_826"  [1 undecoded]
  extrude  "Extruded_827"  [1 undecoded]
  extrude  "Extruded_828"  [1 undecoded]
  extrude  "Extruded_829"  [1 undecoded]
  extrude  "Extruded_830"  [1 undecoded]
  extrude  "Extruded_831"  [1 undecoded]
  extrude  "Extruded_832"  [1 undecoded]
  extrude  "Extruded_833"  [1 undecoded]
  extrude  "Extruded_834"  [1 undecoded]
  extrude  "Extruded_835"  [1 undecoded]
  extrude  "Extruded_836"  [1 undecoded]
  extrude  "Extruded_837"  [1 undecoded]
  extrude  "Extruded_838"  [1 undecoded]
  extrude  "Extruded_839"  [1 undecoded]
  extrude  "Extruded_840"  [1 undecoded]
  extrude  "Extruded_841"  [1 undecoded]
  extrude  "Extruded_842"  [1 undecoded]
  extrude  "Extruded_843"  [1 undecoded]
  extrude  "Extruded_844"  [1 undecoded]
  extrude  "Extruded_845"  [1 undecoded]
  extrude  "Extruded_846"  [1 undecoded]
  extrude  "Extruded_847"  [1 undecoded]
  extrude  "Extruded_848"  [1 undecoded]
  extrude  "Extruded_849"  [1 undecoded]
  extrude  "Extruded_850"  [1 undecoded]
  extrude  "Extruded_851"  [1 undecoded]
  extrude  "Extruded_852"  [1 undecoded]
  extrude  "Extruded_853"  [1 undecoded]
  extrude  "Extruded_854"  [1 undecoded]
  extrude  "Extruded_855"  [1 undecoded]
  extrude  "Extruded_856"  [1 undecoded]
  extrude  "Extruded_857"  [1 undecoded]
  extrude  "Extruded_858"  [1 undecoded]
  extrude  "Extruded_859"  [1 undecoded]
  extrude  "Extruded_860"  [1 undecoded]
  extrude  "Extruded_861"  [1 undecoded]
  extrude  "Extruded_862"  [1 undecoded]
  extrude  "Extruded_863"  [1 undecoded]
  extrude  "Extruded_864"  [1 undecoded]
  extrude  "Extruded_865"  [1 undecoded]
  extrude  "Extruded_866"  [1 undecoded]
  extrude  "Extruded_867"  [1 undecoded]
  extrude  "Extruded_868"  [1 undecoded]
  extrude  "Extruded_869"  [1 undecoded]
  extrude  "Extruded_870"  [1 undecoded]
  extrude  "Extruded_871"  [1 undecoded]
  extrude  "Extruded_872"  [1 undecoded]
  extrude  "Extruded_873"  [1 undecoded]
  extrude  "Extruded_874"  [1 undecoded]
  extrude  "Extruded_875"  [1 undecoded]
  extrude  "Extruded_876"  [1 undecoded]
  extrude  "Extruded_877"  [1 undecoded]
  extrude  "Extruded_878"  [1 undecoded]
  extrude  "Extruded_879"  [1 undecoded]
  extrude  "Extruded_880"  [1 undecoded]
  extrude  "Extruded_881"  [1 undecoded]
  extrude  "Extruded_882"  [1 undecoded]
  extrude  "Extruded_883"  [1 undecoded]
  extrude  "Extruded_884"  [1 undecoded]
  extrude  "Extruded_885"  [1 undecoded]
  extrude  "Extruded_886"  [1 undecoded]
  extrude  "Extruded_887"  [1 undecoded]
  extrude  "Extruded_888"  [1 undecoded]
  extrude  "Extruded_889"  [1 undecoded]
  extrude  "Extruded_890"  [1 undecoded]
  extrude  "Extruded_891"  [1 undecoded]
  extrude  "Extruded_892"  [1 undecoded]
  extrude  "Extruded_893"  [1 undecoded]
  extrude  "Extruded_894"  [1 undecoded]
  extrude  "Extruded_895"  [1 undecoded]
  extrude  "Extruded_896"  [1 undecoded]
  extrude  "Extruded_897"  [1 undecoded]
  extrude  "Extruded_898"  [1 undecoded]
  extrude  "Extruded_899"  [1 undecoded]
  extrude  "Extruded_900"  [1 undecoded]
  extrude  "Extruded_901"  [1 undecoded]
  extrude  "Extruded_902"  [1 undecoded]
  extrude  "Extruded_903"  [1 undecoded]
  extrude  "Extruded_904"  [1 undecoded]
  extrude  "Extruded_905"  [1 undecoded]
  extrude  "Extruded_906"  [1 undecoded]
  extrude  "Extruded_907"  [1 undecoded]
  extrude  "Extruded_908"  [1 undecoded]
  extrude  "Extruded_909"  [1 undecoded]
  extrude  "Extruded_910"  [1 undecoded]
  extrude  "Extruded_911"  [1 undecoded]
  extrude  "Extruded_912"  [1 undecoded]
  extrude  "Extruded_913"  [1 undecoded]
  extrude  "Extruded_914"  [1 undecoded]
  extrude  "Extruded_915"  [1 undecoded]
  extrude  "Extruded_916"  [1 undecoded]
  extrude  "Extruded_917"  [1 undecoded]
  extrude  "Extruded_918"  [1 undecoded]
  extrude  "Extruded_919"  [1 undecoded]
  extrude  "Extruded_920"  [1 undecoded]
  extrude  "Extruded_921"  [1 undecoded]
  extrude  "Extruded_922"  [1 undecoded]
  extrude  "Extruded_923"  [1 undecoded]
  extrude  "Extruded_924"  [1 undecoded]
  extrude  "Extruded_925"  [1 undecoded]
  extrude  "Extruded_926"  [1 undecoded]
  extrude  "Extruded_927"  [1 undecoded]
  extrude  "Extruded_928"  [1 undecoded]
  extrude  "Extruded_929"  [1 undecoded]
  extrude  "Extruded_930"  [1 undecoded]
  extrude  "Extruded_931"  [1 undecoded]
  extrude  "Extruded_932"  [1 undecoded]
  extrude  "Extruded_933"  [1 undecoded]
  extrude  "Extruded_934"  [1 undecoded]
  extrude  "Extruded_935"  [1 undecoded]
  extrude  "Extruded_936"  [1 undecoded]
  extrude  "Extruded_937"  [1 undecoded]
  extrude  "Extruded_938"  [1 undecoded]
  extrude  "Extruded_939"  [1 undecoded]
  extrude  "Extruded_940"  [1 undecoded]
  extrude  "Extruded_941"  [1 undecoded]
  extrude  "Extruded_942"  [1 undecoded]
  extrude  "Extruded_943"  [1 undecoded]
  extrude  "Extruded_944"  [1 undecoded]
  extrude  "Extruded_945"  [1 undecoded]
  extrude  "Extruded_946"  [1 undecoded]
  extrude  "Extruded_947"  [1 undecoded]
  extrude  "Extruded_948"  [1 undecoded]
  extrude  "Extruded_949"  [1 undecoded]
  extrude  "Extruded_950"  [1 undecoded]
  extrude  "Extruded_951"  [1 undecoded]
  extrude  "Extruded_952"  [1 undecoded]
  extrude  "Extruded_953"  [1 undecoded]
  extrude  "Extruded_954"  [1 undecoded]
  extrude  "Extruded_955"  [1 undecoded]
  extrude  "Extruded_956"  [1 undecoded]
  extrude  "Extruded_957"  [1 undecoded]
  extrude  "Extruded_958"  [1 undecoded]
  extrude  "Extruded_959"  [1 undecoded]
  extrude  "Extruded_960"  [1 undecoded]
  extrude  "Extruded_961"  [1 undecoded]
  extrude  "Extruded_962"  [1 undecoded]
  extrude  "Extruded_963"  [1 undecoded]
  extrude  "Extruded_964"  [1 undecoded]
  extrude  "Extruded_965"  [1 undecoded]
  extrude  "Extruded_966"  [1 undecoded]
  extrude  "Extruded_967"  [1 undecoded]
  extrude  "Extruded_968"  [1 undecoded]
  extrude  "Extruded_969"  [1 undecoded]
  extrude  "Extruded_970"  [1 undecoded]
  extrude  "Extruded_971"  [1 undecoded]
  extrude  "Extruded_972"  [1 undecoded]
  extrude  "Extruded_973"  [1 undecoded]
  extrude  "Extruded_974"  [1 undecoded]
  extrude  "Extruded_975"  [1 undecoded]
  extrude  "Extruded_976"  [1 undecoded]
  extrude  "Extruded_977"  [1 undecoded]
  extrude  "Extruded_978"  [1 undecoded]
  extrude  "Extruded_979"  [1 undecoded]
  extrude  "Extruded_980"  [1 undecoded]
  extrude  "Extruded_981"  [1 undecoded]
  extrude  "Extruded_982"  [1 undecoded]
  extrude  "Extruded_983"  [1 undecoded]
  extrude  "Extruded_984"  [1 undecoded]
  extrude  "Extruded_985"  [1 undecoded]
  extrude  "Extruded_986"  [1 undecoded]
  extrude  "Extruded_987"  [1 undecoded]
  extrude  "Extruded_988"  [1 undecoded]
  extrude  "Extruded_989"  [1 undecoded]
  extrude  "Extruded_990"  [1 undecoded]
  extrude  "Extruded_991"  [1 undecoded]
  extrude  "Extruded_992"  [1 undecoded]
  extrude  "Extruded_993"  [1 undecoded]
  extrude  "Extruded_994"  [1 undecoded]
  extrude  "Extruded_995"  [1 undecoded]
  extrude  "Extruded_996"  [1 undecoded]
  extrude  "Extruded_997"  [1 undecoded]
  extrude  "Extruded_998"  [1 undecoded]
  extrude  "Extruded_999"  [1 undecoded]
  extrude  "Extruded_1000"  [1 undecoded]
  extrude  "Extruded_1001"  [1 undecoded]
  extrude  "Extruded_1002"  [1 undecoded]
  extrude  "Extruded_1003"  [1 undecoded]
  extrude  "Extruded_1004"  [1 undecoded]
  extrude  "Extruded_1005"  [1 undecoded]
  extrude  "Extruded_1006"  [1 undecoded]
  extrude  "Extruded_1007"  [1 undecoded]
  extrude  "Extruded_1008"  [1 undecoded]
  extrude  "Extruded_1009"  [1 undecoded]
  extrude  "Extruded_1010"  [1 undecoded]
  extrude  "Extruded_1011"  [1 undecoded]
  extrude  "Extruded_1012"  [1 undecoded]
  extrude  "Extruded_1013"  [1 undecoded]
  extrude  "Extruded_1014"  [1 undecoded]
  extrude  "Extruded_1015"  [1 undecoded]
  extrude  "Extruded_1016"  [1 undecoded]
  extrude  "Extruded_1017"  [1 undecoded]
  extrude  "Extruded_1018"  [1 undecoded]
  other  "Cylinder_31"
  extrude  "Extruded_1019"  [1 undecoded]
  other  "Cylinder_32"
  other  "Cylinder_33"
  extrude  "Extruded_1020"  [1 undecoded]
  other  "Cylinder_34"
  extrude  "Extruded_1021"  [1 undecoded]
  extrude  "Extruded_1022"  [1 undecoded]
  other  "Cylinder_35"
  extrude  "Extruded_1023"  [1 undecoded]
  other  "Cylinder_36"
  other  "Cylinder_37"
  extrude  "Extruded_1024"  [1 undecoded]
  extrude  "Extruded_1025"  [1 undecoded]
  other  "Cylinder_38"
  extrude  "Extruded_1026"  [1 undecoded]
  extrude  "Extruded_1027"  [1 undecoded]
  extrude  "Extruded_1028"  [1 undecoded]
  extrude  "Extruded_1029"  [1 undecoded]
  extrude  "Extruded_1030"  [1 undecoded]
  extrude  "Extruded_1031"  [1 undecoded]
  other  "Cylinder_39"
  extrude  "Extruded_1032"  [1 undecoded]
  extrude  "Extruded_1033"  [1 undecoded]
  other  "Cylinder_40"
  extrude  "Extruded_1034"  [1 undecoded]
  other  "Cylinder_41"
  extrude  "Extruded_1035"  [1 undecoded]
  other  "Cylinder_42"
  extrude  "Extruded_1036"  [1 undecoded]
  other  "Cylinder_43"
  extrude  "Extruded_1037"  [1 undecoded]
  other  "Cylinder_44"
  extrude  "Extruded_1038"  [1 undecoded]
  extrude  "Extruded_1039"  [1 undecoded]
  extrude  "Extruded_1040"  [1 undecoded]
  extrude  "Extruded_1041"  [1 undecoded]
  extrude  "Extruded_1042"  [1 undecoded]
  extrude  "Extruded_1043"  [1 undecoded]
  extrude  "Extruded_1044"  [1 undecoded]
  extrude  "Extruded_1045"  [1 undecoded]
  extrude  "Extruded_1046"  [1 undecoded]
  extrude  "Extruded_1047"  [1 undecoded]
  extrude  "Extruded_1048"  [1 undecoded]
  extrude  "Extruded_1049"  [1 undecoded]
  extrude  "Extruded_1050"  [1 undecoded]
  extrude  "Extruded_1051"  [1 undecoded]
  extrude  "Extruded_1052"  [1 undecoded]
  extrude  "Extruded_1053"  [1 undecoded]
  extrude  "Extruded_1054"  [1 undecoded]
  extrude  "Extruded_1055"  [1 undecoded]
  extrude  "Extruded_1056"  [1 undecoded]
  extrude  "Extruded_1057"  [1 undecoded]
  extrude  "Extruded_1058"  [1 undecoded]
  extrude  "Extruded_1059"  [1 undecoded]
  extrude  "Extruded_1060"  [1 undecoded]
  extrude  "Extruded_1061"  [1 undecoded]
  extrude  "Extruded_1062"  [1 undecoded]
  extrude  "Extruded_1063"  [1 undecoded]
  extrude  "Extruded_1064"  [1 undecoded]
  extrude  "Extruded_1065"  [1 undecoded]
  extrude  "Extruded_1066"  [1 undecoded]
  other  "Cylinder_45"
  extrude  "Extruded_1067"  [1 undecoded]
  extrude  "Extruded_1068"  [1 undecoded]
  extrude  "Extruded_1069"  [1 undecoded]
  extrude  "Extruded_1070"  [1 undecoded]
  extrude  "Extruded_1071"  [1 undecoded]
  extrude  "Extruded_1072"  [1 undecoded]
  extrude  "Extruded_1073"  [1 undecoded]
  extrude  "Extruded_1074"  [1 undecoded]
  extrude  "Extruded_1075"  [1 undecoded]
  extrude  "Extruded_1076"  [1 undecoded]
  extrude  "Extruded_1077"  [1 undecoded]
  extrude  "Extruded_1078"  [1 undecoded]
  extrude  "Extruded_1079"  [1 undecoded]
  extrude  "Extruded_1080"  [1 undecoded]
  extrude  "Extruded_1081"  [1 undecoded]
  extrude  "Extruded_1082"  [1 undecoded]
  extrude  "Extruded_1083"  [1 undecoded]
  extrude  "Extruded_1084"  [1 undecoded]
  extrude  "Extruded_1085"  [1 undecoded]
  extrude  "Extruded_1086"  [1 undecoded]
  extrude  "Extruded_1087"  [1 undecoded]
  extrude  "Extruded_1088"  [1 undecoded]
  extrude  "Extruded_1089"  [1 undecoded]
  extrude  "Extruded_1090"  [1 undecoded]
  extrude  "Extruded_1091"  [1 undecoded]
  extrude  "Extruded_1092"  [1 undecoded]
  extrude  "Extruded_1093"  [1 undecoded]
  extrude  "Extruded_1094"  [1 undecoded]
  extrude  "Extruded_1095"  [1 undecoded]
  extrude  "Extruded_1096"  [1 undecoded]
  extrude  "Extruded_1097"  [1 undecoded]
  extrude  "Extruded_1098"  [1 undecoded]
  extrude  "Extruded_1099"  [1 undecoded]
  extrude  "Extruded_1100"  [1 undecoded]
  extrude  "Extruded_1101"  [1 undecoded]
  extrude  "Extruded_1102"  [1 undecoded]
  extrude  "Extruded_1103"  [1 undecoded]
  extrude  "Extruded_1104"  [1 undecoded]
  extrude  "Extruded_1105"  [1 undecoded]
  extrude  "Extruded_1106"  [1 undecoded]
  extrude  "Extruded_1107"  [1 undecoded]
  extrude  "Extruded_1108"  [1 undecoded]
  extrude  "Extruded_1109"  [1 undecoded]
  extrude  "Extruded_1110"  [1 undecoded]
  extrude  "Extruded_1111"  [1 undecoded]
  sketch  "3D Sketch1"
  projected_geometry  "Projected Loop1"
  projected_geometry  "Projected Loop2"
  projected_geometry  "Projected Loop3"
  projected_geometry  "Projected Loop4"
  projected_geometry  "Projected Loop5"
  projected_geometry  "Projected Loop6"
  projected_geometry  "Projected Loop7"
  projected_geometry  "Projected Loop8"
  projected_geometry  "Projected Loop9"
  projected_geometry  "Projected Loop10"
  projected_geometry  "Projected Loop11"
  projected_geometry  "Projected Loop12"
  projected_geometry  "Projected Loop13"
  projected_geometry  "Projected Loop14"
  projected_geometry  "Projected Loop15"
  projected_geometry  "Projected Loop16"
  projected_geometry  "Projected Loop17"
  projected_geometry  "Projected Loop18"
  projected_geometry  "Projected Loop19"
  projected_geometry  "Projected Loop20"
  projected_geometry  "Projected Loop21"
  imported_body  "Base1"
  imported_body  "Base2"
  imported_body  "Base3"
  imported_body  "Base4"
  imported_body  "Base5"
  imported_body  "Base6"
  imported_body  "Base7"
  imported_body  "Base8"
  imported_body  "Base9"
  imported_body  "Base10"
  imported_body  "Base11"
  imported_body  "Base12"
  imported_body  "Base13"
  imported_body  "Base14"
  imported_body  "Base15"
  imported_body  "Base16"
  imported_body  "Base17"
  imported_body  "Base18"
  imported_body  "Base19"
  imported_body  "Base20"
  imported_body  "Base21"
  imported_body  "Base22"
  imported_body  "Base23"
  imported_body  "Base24"
  imported_body  "Base25"
  imported_body  "Base26"
  imported_body  "Base27"
  imported_body  "Base28"
  imported_body  "Base29"
  imported_body  "Base30"
  imported_body  "Base31"
  imported_body  "Base32"
  imported_body  "Base33"
  imported_body  "Base34"
  imported_body  "Base35"
  imported_body  "Base36"
  imported_body  "Base37"
  imported_body  "Base38"
  imported_body  "Base39"
  imported_body  "Base40"
  imported_body  "Base41"
  imported_body  "Base42"
  imported_body  "Base43"
  imported_body  "Base44"
  imported_body  "Base45"
  imported_body  "Base46"
  imported_body  "Base47"
  imported_body  "Base48"
  imported_body  "Base49"
  imported_body  "Base50"
  imported_body  "Base51"
  imported_body  "Base52"
  imported_body  "Base53"
  imported_body  "Base54"
  imported_body  "Base55"
  imported_body  "Base56"
  imported_body  "Base57"
  imported_body  "Base58"
  imported_body  "Base59"
  imported_body  "Base60"
  imported_body  "Base61"
  imported_body  "Base62"
  imported_body  "Base63"
  imported_body  "Base64"
  imported_body  "Base65"
  imported_body  "Base66"
  imported_body  "Base67"
  imported_body  "Base68"
  imported_body  "Base69"
  imported_body  "Base70"
  imported_body  "Base71"
  imported_body  "Base72"
  imported_body  "Base73"
  imported_body  "Base74"
  imported_body  "Base75"
  imported_body  "Base76"
  imported_body  "Base77"
  imported_body  "Base78"
  imported_body  "Base79"
  imported_body  "Base80"
  imported_body  "Base81"
  imported_body  "Base82"
  imported_body  "Base83"
  imported_body  "Base84"
  imported_body  "Base85"
  imported_body  "Base86"
  imported_body  "Base87"
  imported_body  "Base88"
  imported_body  "Base89"
  imported_body  "Base90"
  imported_body  "Base91"
  imported_body  "Base92"
  imported_body  "Base93"
  imported_body  "Base94"
  imported_body  "Base95"
  imported_body  "Base96"
  imported_body  "Base97"
  imported_body  "Base98"
  imported_body  "Base99"
  imported_body  "Base100"
  imported_body  "Base101"
  imported_body  "Base102"
  imported_body  "Base103"
  imported_body  "Base104"
  imported_body  "Base105"
  imported_body  "Base106"
  imported_body  "Base107"
  imported_body  "Base108"
  imported_body  "Base109"
  imported_body  "Base110"
  imported_body  "Base111"
  imported_body  "Base112"
  imported_body  "Base113"
  imported_body  "Base114"
  imported_body  "Base115"
  imported_body  "Base116"
  imported_body  "Base117"
  imported_body  "Base118"
  imported_body  "Base119"
  imported_body  "Base120"
  imported_body  "Base121"
  imported_body  "Base122"
  imported_body  "Base123"
  imported_body  "Base124"
  imported_body  "Base125"
  imported_body  "Base126"
  imported_body  "Base127"
  imported_body  "Base128"
  imported_body  "Base129"
  imported_body  "Base130"
  imported_body  "Base131"
  imported_body  "Base132"
  imported_body  "Base133"
  imported_body  "Base134"
  imported_body  "Base135"
  imported_body  "Base136"
  imported_body  "Base137"
  imported_body  "Base138"
  imported_body  "Base139"
  imported_body  "Base140"
  imported_body  "Base141"
  imported_body  "Base142"
  imported_body  "Base143"
  imported_body  "Base144"
  imported_body  "Base145"
  imported_body  "Base146"
  imported_body  "Base147"
  imported_body  "Base148"
  imported_body  "Base149"
  imported_body  "Base150"
  imported_body  "Base151"
  imported_body  "Base152"
  imported_body  "Base153"
  imported_body  "Base154"
  imported_body  "Base155"
  imported_body  "Base156"
  imported_body  "Base157"
  imported_body  "Base158"
  imported_body  "Base159"
  imported_body  "Base160"
  imported_body  "Base161"
  imported_body  "Base162"
  imported_body  "Base163"
  imported_body  "Base164"
  imported_body  "Base165"
  imported_body  "Base166"
  imported_body  "Base167"
  imported_body  "Base168"
  imported_body  "Base169"
  imported_body  "Base170"
  imported_body  "Base171"
  imported_body  "Base172"
  imported_body  "Base173"
  imported_body  "Base174"
  imported_body  "Base175"
  imported_body  "Base176"
  imported_body  "Base177"
  imported_body  "Base178"
  imported_body  "Base179"
  imported_body  "Base180"
  imported_body  "Base181"
  imported_body  "Base182"
  imported_body  "Base183"
  imported_body  "Base184"
  imported_body  "Base185"
  imported_body  "Base186"
  imported_body  "Base187"
  imported_body  "Base188"
  imported_body  "Base189"
  imported_body  "Base190"
  imported_body  "Base191"
  imported_body  "Base192"
  imported_body  "Base193"
  imported_body  "Base194"
  imported_body  "Base195"
  imported_body  "Base196"
  imported_body  "Base197"
  imported_body  "Base198"
  imported_body  "Base199"
  imported_body  "Base200"
  imported_body  "Base201"
  imported_body  "Base202"
  imported_body  "Base203"
  imported_body  "Base204"
  imported_body  "Base205"
  imported_body  "Base206"
  imported_body  "Base207"
  imported_body  "Base208"
  imported_body  "Base209"
  imported_body  "Base210"
  imported_body  "Base211"
  imported_body  "Base212"
  imported_body  "Base213"
  imported_body  "Base214"
  imported_body  "Base215"
  imported_body  "Base216"
  imported_body  "Base217"
  imported_body  "Base218"
  imported_body  "Base219"
  imported_body  "Base220"
  imported_body  "Base221"
  imported_body  "Base222"
  imported_body  "Base223"
  imported_body  "Base224"
  imported_body  "Base225"
  imported_body  "Base226"
  imported_body  "Base227"
  imported_body  "Base228"
  imported_body  "Base229"
  imported_body  "Base230"
  imported_body  "Base231"
  imported_body  "Base232"
  imported_body  "Base233"
  imported_body  "Base234"
  imported_body  "Base235"
  imported_body  "Base236"
  imported_body  "Base237"
  imported_body  "Base238"
  imported_body  "Base239"
  imported_body  "Base240"
  imported_body  "Base241"
  imported_body  "Base242"
  imported_body  "Base243"
  imported_body  "Base244"
  imported_body  "Base245"
  imported_body  "Base246"
  imported_body  "Base247"
  imported_body  "Base248"
  imported_body  "Base249"
  imported_body  "Base250"
  imported_body  "Base251"
  imported_body  "Base252"
  imported_body  "Base253"
  imported_body  "Base254"
  imported_body  "Base255"
  imported_body  "Base256"
  imported_body  "Base257"
  imported_body  "Base258"
  imported_body  "Base259"
  imported_body  "Base260"
  imported_body  "Base261"
  imported_body  "Base262"
  imported_body  "Base263"
  imported_body  "Base264"
  imported_body  "Base265"
  imported_body  "Base266"
  imported_body  "Base267"
  imported_body  "Base268"
  imported_body  "Base269"
  imported_body  "Base270"
  imported_body  "Base271"
  imported_body  "Base272"
  imported_body  "Base273"
  imported_body  "Base274"
  imported_body  "Base275"
  imported_body  "Base276"
  imported_body  "Base277"
  imported_body  "Base278"
  imported_body  "Base279"
  imported_body  "Base280"
  imported_body  "Base281"
  imported_body  "Base282"
  imported_body  "Base283"
  imported_body  "Base284"
  imported_body  "Base285"
  imported_body  "Base286"
  imported_body  "Base287"
  imported_body  "Base288"
  imported_body  "Base289"
  imported_body  "Base290"
  imported_body  "Base291"
  imported_body  "Base292"
  imported_body  "Base293"
  imported_body  "Base294"
  imported_body  "Base295"
  imported_body  "Base296"
  imported_body  "Base297"
  imported_body  "Base298"
  imported_body  "Base299"
  imported_body  "Base300"
  imported_body  "Base301"
  imported_body  "Base302"
  imported_body  "Base303"
  imported_body  "Base304"
  imported_body  "Base305"
  imported_body  "Base306"
  imported_body  "Base307"
  imported_body  "Base308"
  imported_body  "Base309"
  imported_body  "Base310"
  imported_body  "Base311"
  imported_body  "Base312"
  imported_body  "Base313"
  imported_body  "Base314"
  imported_body  "Base315"
  imported_body  "Base316"
  imported_body  "Base317"
  imported_body  "Base318"
  imported_body  "Base319"
  imported_body  "Base320"
  imported_body  "Base321"
  imported_body  "Base322"
  imported_body  "Base323"
  imported_body  "Base324"
  imported_body  "Base325"
  imported_body  "Base326"
  imported_body  "Base327"
  imported_body  "Base328"
  imported_body  "Base329"
  imported_body  "Base330"
  imported_body  "Base331"
  imported_body  "Base332"
  imported_body  "Base333"
  imported_body  "Base334"
  imported_body  "Base335"
  imported_body  "Base336"
  imported_body  "Base337"
  imported_body  "Base338"
  imported_body  "Base339"
  imported_body  "Base340"
  imported_body  "Base341"
  imported_body  "Base342"
  imported_body  "Base343"
  imported_body  "Base344"
  imported_body  "Base345"
  imported_body  "Base346"
  imported_body  "Base347"
  imported_body  "Base348"
  imported_body  "Base349"
  imported_body  "Base350"
  imported_body  "Base351"
  imported_body  "Base352"
  imported_body  "Base353"
  imported_body  "Base354"
  imported_body  "Base355"
  imported_body  "Base356"
  imported_body  "Base357"
  imported_body  "Base358"
  imported_body  "Base359"
  imported_body  "Base360"
  imported_body  "Base361"
  imported_body  "Base362"
  imported_body  "Base363"
  imported_body  "Base364"
  imported_body  "Base365"
  imported_body  "Base366"
  imported_body  "Base367"
  imported_body  "Base368"
  imported_body  "Base369"
  imported_body  "Base370"
  imported_body  "Base371"
  imported_body  "Base372"
  imported_body  "Base373"
  imported_body  "Base374"
  imported_body  "Base375"
  imported_body  "Base376"
  imported_body  "Base377"
  imported_body  "Base378"
  imported_body  "Base379"
  imported_body  "Base380"
  imported_body  "Base381"
  imported_body  "Base382"
  imported_body  "Base383"
  imported_body  "Base384"
  imported_body  "Base385"
  imported_body  "Base386"
  imported_body  "Base387"
  imported_body  "Base388"
  imported_body  "Base389"
  imported_body  "Base390"
  imported_body  "Base391"
  imported_body  "Base392"
  imported_body  "Base393"
  imported_body  "Base394"
  imported_body  "Base395"
  imported_body  "Base396"
  imported_body  "Base397"
  imported_body  "Base398"
  imported_body  "Base399"
  imported_body  "Base400"
  imported_body  "Base401"
  imported_body  "Base402"
  imported_body  "Base403"
  imported_body  "Base404"
  imported_body  "Base405"
  imported_body  "Base406"
  imported_body  "Base407"
  imported_body  "Base408"
  imported_body  "Base409"
  imported_body  "Base410"
  imported_body  "Base411"
  imported_body  "Base412"
  imported_body  "Base413"
  imported_body  "Base414"
  imported_body  "Base415"
  imported_body  "Base416"
  imported_body  "Base417"
  imported_body  "Base418"
  imported_body  "Base419"
  imported_body  "Base420"
  imported_body  "Base421"
  imported_body  "Base422"
  imported_body  "Base423"
  imported_body  "Base424"
  imported_body  "Base425"
  imported_body  "Base426"
  imported_body  "Base427"
  imported_body  "Base428"
  imported_body  "Base429"
  imported_body  "Base430"
  imported_body  "Base431"
  imported_body  "Base432"
  imported_body  "Base433"
  imported_body  "Base434"
  imported_body  "Base435"
  imported_body  "Base436"
  imported_body  "Base437"
  imported_body  "Base438"
  imported_body  "Base439"
  imported_body  "Base440"
  imported_body  "Base441"
  imported_body  "Base442"
  imported_body  "Base443"
  imported_body  "Base444"
  imported_body  "Base445"
  imported_body  "Base446"
  imported_body  "Base447"
  imported_body  "Base448"
  imported_body  "Base449"
  imported_body  "Base450"
  imported_body  "Base451"
  imported_body  "Base452"
  imported_body  "Base453"
  imported_body  "Base454"
  imported_body  "Base455"
  imported_body  "Base456"
  imported_body  "Base457"
  imported_body  "Base458"
  imported_body  "Base459"
  imported_body  "Base460"
  imported_body  "Base461"
  imported_body  "Base462"
  imported_body  "Base463"
  imported_body  "Base464"
  imported_body  "Base465"
  imported_body  "Base466"
  imported_body  "Base467"
  imported_body  "Base468"
  imported_body  "Base469"
  imported_body  "Base470"
  imported_body  "Base471"
  imported_body  "Base472"
  imported_body  "Base473"
  imported_body  "Base474"
  imported_body  "Base475"
  imported_body  "Base476"
  imported_body  "Base477"
  imported_body  "Base478"
  imported_body  "Base479"
  imported_body  "Base480"
  imported_body  "Base481"
  imported_body  "Base482"
  imported_body  "Base483"
  imported_body  "Base484"
  imported_body  "Base485"
  imported_body  "Base486"
  imported_body  "Base487"
  imported_body  "Base488"
  imported_body  "Base489"
  imported_body  "Base490"
  imported_body  "Base491"
  imported_body  "Base492"
  imported_body  "Base493"
  imported_body  "Base494"
  imported_body  "Base495"
  imported_body  "Base496"
  imported_body  "Base497"
  imported_body  "Base498"
  imported_body  "Base499"
  imported_body  "Base500"
  imported_body  "Base501"
  imported_body  "Base502"
  imported_body  "Base503"
  imported_body  "Base504"
  imported_body  "Base505"
  imported_body  "Base506"
  imported_body  "Base507"
  imported_body  "Base508"
  imported_body  "Base509"
  imported_body  "Base510"
  imported_body  "Base511"
  imported_body  "Base512"
  imported_body  "Base513"
  imported_body  "Base514"
  imported_body  "Base515"
  imported_body  "Base516"
  imported_body  "Base517"
  imported_body  "Base518"
  imported_body  "Base519"
  imported_body  "Base520"
  imported_body  "Base521"
  imported_body  "Base522"
  imported_body  "Base523"
  imported_body  "Base524"
  imported_body  "Base525"
  imported_body  "Base526"
  imported_body  "Base527"
  imported_body  "Base528"
  imported_body  "Base529"
  imported_body  "Base530"
  imported_body  "Base531"
  imported_body  "Base532"
  imported_body  "Base533"
  imported_body  "Base534"
  imported_body  "Base535"
  imported_body  "Base536"
  imported_body  "Base537"
  imported_body  "Base538"
  imported_body  "Base539"
  imported_body  "Base540"
  imported_body  "Base541"
  imported_body  "Base542"
  imported_body  "Base543"
  imported_body  "Base544"
  imported_body  "Base545"
  imported_body  "Base546"
  imported_body  "Base547"
  imported_body  "Base548"
  imported_body  "Base549"
  imported_body  "Base550"
  imported_body  "Base551"
  imported_body  "Base552"
  imported_body  "Base553"
  imported_body  "Base554"
  imported_body  "Base555"
  imported_body  "Base556"
  imported_body  "Base557"
  imported_body  "Base558"
  imported_body  "Base559"
  imported_body  "Base560"
  imported_body  "Base561"
  imported_body  "Base562"
  imported_body  "Base563"
  imported_body  "Base564"
  imported_body  "Base565"
  imported_body  "Base566"
  imported_body  "Base567"
  imported_body  "Base568"
  imported_body  "Base569"
  imported_body  "Base570"
  imported_body  "Base571"
  imported_body  "Base572"
  imported_body  "Base573"
  imported_body  "Base574"
  imported_body  "Base575"
  imported_body  "Base576"
  imported_body  "Base577"
  imported_body  "Base578"
  imported_body  "Base579"
  imported_body  "Base580"
  imported_body  "Base581"
  imported_body  "Base582"
  imported_body  "Base583"
  imported_body  "Base584"
  imported_body  "Base585"
  imported_body  "Base586"
  imported_body  "Base587"
  imported_body  "Base588"
  imported_body  "Base589"
  imported_body  "Base590"
  imported_body  "Base591"
  imported_body  "Base592"
  imported_body  "Base593"
  imported_body  "Base594"
  imported_body  "Base595"
  imported_body  "Base596"
  imported_body  "Base597"
  imported_body  "Base598"
  imported_body  "Base599"
  imported_body  "Base600"
  imported_body  "Base601"
  imported_body  "Base602"
  imported_body  "Base603"
  imported_body  "Base604"
  imported_body  "Base605"
  imported_body  "Base606"
  imported_body  "Base607"
  imported_body  "Base608"
  imported_body  "Base609"
  imported_body  "Base610"
  imported_body  "Base611"
  imported_body  "Base612"
  imported_body  "Base613"
  imported_body  "Base614"
  imported_body  "Base615"
  imported_body  "Base616"
  imported_body  "Base617"
  imported_body  "Base618"
  imported_body  "Base619"
  imported_body  "Base620"
  imported_body  "Base621"
  imported_body  "Base622"
  imported_body  "Base623"
  imported_body  "Base624"
  imported_body  "Base625"
  imported_body  "Base626"
  imported_body  "Base627"
  imported_body  "Base628"
  imported_body  "Base629"
  imported_body  "Base630"
  imported_body  "Base631"
  imported_body  "Base632"
  imported_body  "Base633"
  imported_body  "Base634"
  imported_body  "Base635"
  imported_body  "Base636"
  imported_body  "Base637"
  imported_body  "Base638"
  imported_body  "Base639"
  imported_body  "Base640"
  imported_body  "Base641"
  imported_body  "Base642"
  imported_body  "Base643"
  imported_body  "Base644"
  imported_body  "Base645"
  imported_body  "Base646"
  imported_body  "Base647"
  imported_body  "Base648"
  imported_body  "Base649"
  imported_body  "Base650"
  imported_body  "Base651"
  imported_body  "Base652"
  imported_body  "Base653"
  imported_body  "Base654"
  imported_body  "Base655"
  imported_body  "Base656"
  imported_body  "Base657"
  imported_body  "Base658"
  imported_body  "Base659"
  imported_body  "Base660"
  imported_body  "Base661"
  imported_body  "Base662"
  imported_body  "Base663"
  imported_body  "Base664"
  imported_body  "Base665"
  imported_body  "Base666"
  imported_body  "Base667"
  imported_body  "Base668"
  imported_body  "Base669"
  imported_body  "Base670"
  imported_body  "Base671"
  imported_body  "Base672"
  imported_body  "Base673"
  imported_body  "Base674"
  imported_body  "Base675"
  imported_body  "Base676"
  imported_body  "Base677"
  imported_body  "Base678"
  imported_body  "Base679"
  imported_body  "Base680"
  imported_body  "Base681"
  imported_body  "Base682"
  imported_body  "Base683"
  imported_body  "Base684"
  imported_body  "Base685"
  imported_body  "Base686"
  imported_body  "Base687"
  imported_body  "Base688"
  imported_body  "Base689"
  imported_body  "Base690"
  imported_body  "Base691"
  imported_body  "Base692"
  imported_body  "Base693"
  imported_body  "Base694"
  imported_body  "Base695"
  imported_body  "Base696"
  imported_body  "Base697"
  imported_body  "Base698"
  imported_body  "Base699"
  imported_body  "Base700"
  imported_body  "Base701"
  imported_body  "Base702"
  imported_body  "Base703"
  imported_body  "Base704"
  imported_body  "Base705"
  imported_body  "Base706"
  imported_body  "Base707"
  imported_body  "Base708"
  imported_body  "Base709"
  imported_body  "Base710"
  imported_body  "Base711"
  imported_body  "Base712"
  imported_body  "Base713"
  imported_body  "Base714"
  imported_body  "Base715"
  imported_body  "Base716"
  imported_body  "Base717"
  imported_body  "Base718"
  imported_body  "Base719"
  imported_body  "Base720"
  imported_body  "Base721"
  imported_body  "Base722"
  imported_body  "Base723"
  imported_body  "Base724"
  imported_body  "Base725"
  imported_body  "Base726"
  imported_body  "Base727"
  imported_body  "Base728"
  imported_body  "Base729"
  imported_body  "Base730"
  imported_body  "Base731"
  imported_body  "Base732"
  imported_body  "Base733"
  imported_body  "Base734"
  imported_body  "Base735"
  imported_body  "Base736"
  imported_body  "Base737"
  imported_body  "Base738"
  imported_body  "Base739"
  imported_body  "Base740"
  imported_body  "Base741"
  imported_body  "Base742"
  imported_body  "Base743"
  imported_body  "Base744"
  imported_body  "Base745"
  imported_body  "Base746"
  imported_body  "Base747"
  imported_body  "Base748"
  imported_body  "Base749"
  imported_body  "Base750"
  imported_body  "Base751"
  imported_body  "Base752"
  imported_body  "Base753"
  imported_body  "Base754"
  imported_body  "Base755"
  imported_body  "Base756"
  imported_body  "Base757"
  imported_body  "Base758"
  imported_body  "Base759"
  imported_body  "Base760"
  imported_body  "Base761"
  imported_body  "Base762"
  imported_body  "Base763"
  imported_body  "Base764"
  imported_body  "Base765"
  imported_body  "Base766"
  imported_body  "Base767"
  imported_body  "Base768"
  imported_body  "Base769"
  imported_body  "Base770"
  imported_body  "Base771"
  imported_body  "Base772"
  imported_body  "Base773"
  imported_body  "Base774"
  imported_body  "Base775"
  imported_body  "Base776"
  imported_body  "Base777"
  imported_body  "Base778"
  imported_body  "Base779"
  imported_body  "Base780"
  imported_body  "Base781"
  imported_body  "Base782"
  imported_body  "Base783"
  imported_body  "Base784"
  imported_body  "Base785"
  imported_body  "Base786"
  imported_body  "Base787"
  imported_body  "Base788"
  imported_body  "Base789"
  imported_body  "Base790"
  imported_body  "Base791"
  imported_body  "Base792"
  imported_body  "Base793"
  imported_body  "Base794"
  imported_body  "Base795"
  imported_body  "Base796"
  imported_body  "Base797"
  imported_body  "Base798"
  imported_body  "Base799"
  imported_body  "Base800"
  imported_body  "Base801"
  imported_body  "Base802"
  imported_body  "Base803"
  imported_body  "Base804"
  imported_body  "Base805"
  imported_body  "Base806"
  imported_body  "Base807"
  imported_body  "Base808"
  imported_body  "Base809"
  imported_body  "Base810"
  imported_body  "Base811"
  imported_body  "Base812"
  imported_body  "Base813"
  imported_body  "Base814"
  imported_body  "Base815"
  imported_body  "Base816"
  imported_body  "Base817"
  imported_body  "Base818"
  imported_body  "Base819"
  imported_body  "Base820"
  imported_body  "Base821"
  imported_body  "Base822"
  imported_body  "Base823"
  imported_body  "Base824"
  imported_body  "Base825"
  imported_body  "Base826"
  imported_body  "Base827"
  imported_body  "Base828"
  imported_body  "Base829"
  imported_body  "Base830"
  imported_body  "Base831"
  imported_body  "Base832"
  imported_body  "Base833"
  imported_body  "Base834"
  imported_body  "Base835"
  imported_body  "Base836"
  imported_body  "Base837"
  imported_body  "Base838"
  imported_body  "Base839"
  imported_body  "Base840"
  imported_body  "Base841"
  imported_body  "Base842"
  imported_body  "Base843"
  imported_body  "Base844"
  imported_body  "Base845"
  imported_body  "Base846"
  imported_body  "Base847"
  imported_body  "Base848"
  imported_body  "Base849"
  imported_body  "Base850"
  imported_body  "Base851"
  imported_body  "Base852"
  imported_body  "Base853"
  imported_body  "Base854"
  imported_body  "Base855"
  imported_body  "Base856"
  imported_body  "Base857"
  imported_body  "Base858"
  imported_body  "Base859"
  imported_body  "Base860"
  imported_body  "Base861"
  imported_body  "Base862"
  imported_body  "Base863"
  imported_body  "Base864"
  imported_body  "Base865"
  imported_body  "Base866"
  imported_body  "Base867"
  imported_body  "Base868"
  imported_body  "Base869"
  imported_body  "Base870"
  imported_body  "Base871"
  imported_body  "Base872"
  imported_body  "Base873"
  imported_body  "Base874"
  imported_body  "Base875"
  imported_body  "Base876"
  imported_body  "Base877"
  imported_body  "Base878"
  imported_body  "Base879"
  imported_body  "Base880"
  imported_body  "Base881"
  imported_body  "Base882"
  imported_body  "Base883"
  imported_body  "Base884"
  imported_body  "Base885"
  imported_body  "Base886"
  imported_body  "Base887"
  imported_body  "Base888"
  imported_body  "Base889"
  imported_body  "Base890"
  imported_body  "Base891"
  imported_body  "Base892"
  imported_body  "Base893"
  imported_body  "Base894"
  imported_body  "Base895"
  imported_body  "Base896"
  imported_body  "Base897"
  imported_body  "Base898"
  imported_body  "Base899"
  imported_body  "Base900"
  imported_body  "Base901"
  imported_body  "Base902"
  imported_body  "Base903"
  imported_body  "Base904"
  imported_body  "Base905"
  imported_body  "Base906"
  imported_body  "Base907"
  imported_body  "Base908"
  imported_body  "Base909"
  imported_body  "Base910"
  imported_body  "Base911"
  imported_body  "Base912"
  imported_body  "Base913"
  imported_body  "Base914"
  imported_body  "Base915"
  imported_body  "Base916"
  imported_body  "Base917"
  imported_body  "Base918"
  imported_body  "Base919"
  imported_body  "Base920"
  imported_body  "Base921"
  imported_body  "Base922"
  imported_body  "Base923"
  imported_body  "Base924"
  imported_body  "Base925"
  imported_body  "Base926"
  imported_body  "Base927"
  imported_body  "Base928"
  imported_body  "Base929"
  imported_body  "Base930"
  imported_body  "Base931"
  imported_body  "Base932"
  imported_body  "Base933"
  imported_body  "Base934"
  imported_body  "Base935"
  imported_body  "Base936"
  imported_body  "Base937"
  imported_body  "Base938"
  imported_body  "Base939"
  imported_body  "Base940"
  imported_body  "Base941"
  imported_body  "Base942"
  imported_body  "Base943"
  imported_body  "Base944"
  imported_body  "Base945"
  imported_body  "Base946"
  imported_body  "Base947"
  imported_body  "Base948"
  imported_body  "Base949"
  imported_body  "Base950"
  imported_body  "Base951"
  imported_body  "Base952"
  imported_body  "Base953"
  imported_body  "Base954"
  imported_body  "Base955"
  imported_body  "Base956"
  imported_body  "Base957"
  imported_body  "Base958"
  imported_body  "Base959"
  imported_body  "Base960"
  imported_body  "Base961"
  imported_body  "Base962"
  imported_body  "Base963"
  imported_body  "Base964"
  imported_body  "Base965"
  imported_body  "Base966"
  imported_body  "Base967"
  imported_body  "Base968"
  imported_body  "Base969"
  imported_body  "Base970"
  imported_body  "Base971"
  imported_body  "Base972"
  imported_body  "Base973"
  imported_body  "Base974"
  imported_body  "Base975"
  imported_body  "Base976"
  imported_body  "Base977"
  imported_body  "Base978"
  imported_body  "Base979"
  imported_body  "Base980"
  imported_body  "Base981"
  imported_body  "Base982"
  imported_body  "Base983"
  imported_body  "Base984"
  imported_body  "Base985"
  imported_body  "Base986"
  imported_body  "Base987"
  imported_body  "Base988"
  imported_body  "Base989"
  imported_body  "Base990"
  imported_body  "Base991"
  imported_body  "Base992"
  imported_body  "Base993"
  imported_body  "Base994"
  imported_body  "Base995"
  imported_body  "Base996"
  imported_body  "Base997"
  imported_body  "Base998"
  imported_body  "Base999"
  imported_body  "Base1000"
  imported_body  "Base1001"
  imported_body  "Base1002"
  imported_body  "Base1003"
  imported_body  "Base1004"
  imported_body  "Base1005"
  imported_body  "Base1006"
  imported_body  "Base1007"
  imported_body  "Base1008"
  imported_body  "Base1009"
  imported_body  "Base1010"
  imported_body  "Base1011"
  imported_body  "Base1012"
  imported_body  "Base1013"
  imported_body  "Base1014"
  imported_body  "Base1015"
  imported_body  "Base1016"
  imported_body  "Base1017"
  imported_body  "Base1018"
  imported_body  "Base1019"
  imported_body  "Base1020"
  imported_body  "Base1021"
  imported_body  "Base1022"
  imported_body  "Base1023"
  imported_body  "Base1024"
  imported_body  "Base1025"
  imported_body  "Base1026"
  imported_body  "Base1027"
  imported_body  "Base1028"
  imported_body  "Base1029"
  imported_body  "Base1030"
  imported_body  "Base1031"
  imported_body  "Base1032"
  imported_body  "Base1033"
  imported_body  "Base1034"
  imported_body  "Base1035"
  imported_body  "Base1036"
  imported_body  "Base1037"
  imported_body  "Base1038"
  imported_body  "Base1039"
  imported_body  "Base1040"
  imported_body  "Base1041"
  imported_body  "Base1042"
  imported_body  "Base1043"
  imported_body  "Base1044"
  imported_body  "Base1045"
  imported_body  "Base1046"
  imported_body  "Base1047"
  imported_body  "Base1048"
  imported_body  "Base1049"
  imported_body  "Base1050"
  imported_body  "Base1051"
  imported_body  "Base1052"
  imported_body  "Base1053"
  imported_body  "Base1054"
  imported_body  "Base1055"
  imported_body  "Base1056"
  imported_body  "Base1057"
  imported_body  "Base1058"
  imported_body  "Base1059"
  imported_body  "Base1060"
  imported_body  "Base1061"
  imported_body  "Base1062"
  imported_body  "Base1063"
  imported_body  "Base1064"
  imported_body  "Base1065"
  imported_body  "Base1066"
  imported_body  "Base1067"
  imported_body  "Base1068"
  imported_body  "Base1069"
  imported_body  "Base1070"
  imported_body  "Base1071"
  imported_body  "Base1072"
  imported_body  "Base1073"
  imported_body  "Base1074"
  imported_body  "Base1075"
  imported_body  "Base1076"
  imported_body  "Base1077"
  imported_body  "Base1078"
  imported_body  "Base1079"
  imported_body  "Base1080"
  imported_body  "Base1081"
  imported_body  "Base1082"
  imported_body  "Base1083"
  imported_body  "Base1084"
  imported_body  "Base1085"
  imported_body  "Base1086"
  imported_body  "Base1087"
  imported_body  "Base1088"
  imported_body  "Base1089"
  imported_body  "Base1090"
  imported_body  "Base1091"
  imported_body  "Base1092"
  imported_body  "Base1093"
  imported_body  "Base1094"
  imported_body  "Base1095"
  imported_body  "Base1096"
  imported_body  "Base1097"
  imported_body  "Base1098"
  imported_body  "Base1099"
  imported_body  "Base1100"
  imported_body  "Base1101"
  imported_body  "Base1102"
  imported_body  "Base1103"
  imported_body  "Base1104"
  imported_body  "Base1105"
  imported_body  "Base1106"
  imported_body  "Base1107"
  imported_body  "Base1108"
  imported_body  "Base1109"
  imported_body  "Base1110"
  imported_body  "Base1111"
  imported_body  "Base1112"
  imported_body  "Base1113"
  imported_body  "Base1114"
  imported_body  "Base1115"
  imported_body  "Base1116"
  imported_body  "Base1117"
  imported_body  "Base1118"
  imported_body  "Base1119"
  imported_body  "Base1120"
  imported_body  "Base1121"
  imported_body  "Base1122"
  imported_body  "Base1123"
  imported_body  "Base1124"
  imported_body  "Base1125"
  imported_body  "Base1126"
  imported_body  "Base1127"
  imported_body  "Base1128"
  imported_body  "Base1129"
  imported_body  "Base1130"
  imported_body  "Base1131"
  imported_body  "Base1132"
  imported_body  "Base1133"
  imported_body  "Base1134"
  imported_body  "Base1135"
  imported_body  "Base1136"
  imported_body  "Base1137"
  imported_body  "Base1138"
  imported_body  "Base1139"
  imported_body  "Base1140"
  imported_body  "Base1141"
  imported_body  "Base1142"
  imported_body  "Base1143"
  imported_body  "Base1144"
  imported_body  "Base1145"
  imported_body  "Base1146"
  imported_body  "Base1147"
  imported_body  "Base1148"
  imported_body  "Base1149"
  imported_body  "Base1150"
  imported_body  "Base1151"
  imported_body  "Base1152"
  imported_body  "Base1153"
  imported_body  "Base1154"
  imported_body  "Base1155"
  imported_body  "Base1156"
  imported_body  "Base1157"
  imported_body  "Base1158"
  imported_body  "Base1159"
  imported_body  "Base1160"
  imported_body  "Base1161"
  imported_body  "Base1162"
  imported_body  "Base1163"
note: 1097 required parameter values undecoded (feature->parameter linkage not recoverable at this tier; creation-order binding heuristic only, values carry confidence <= 0.55)
